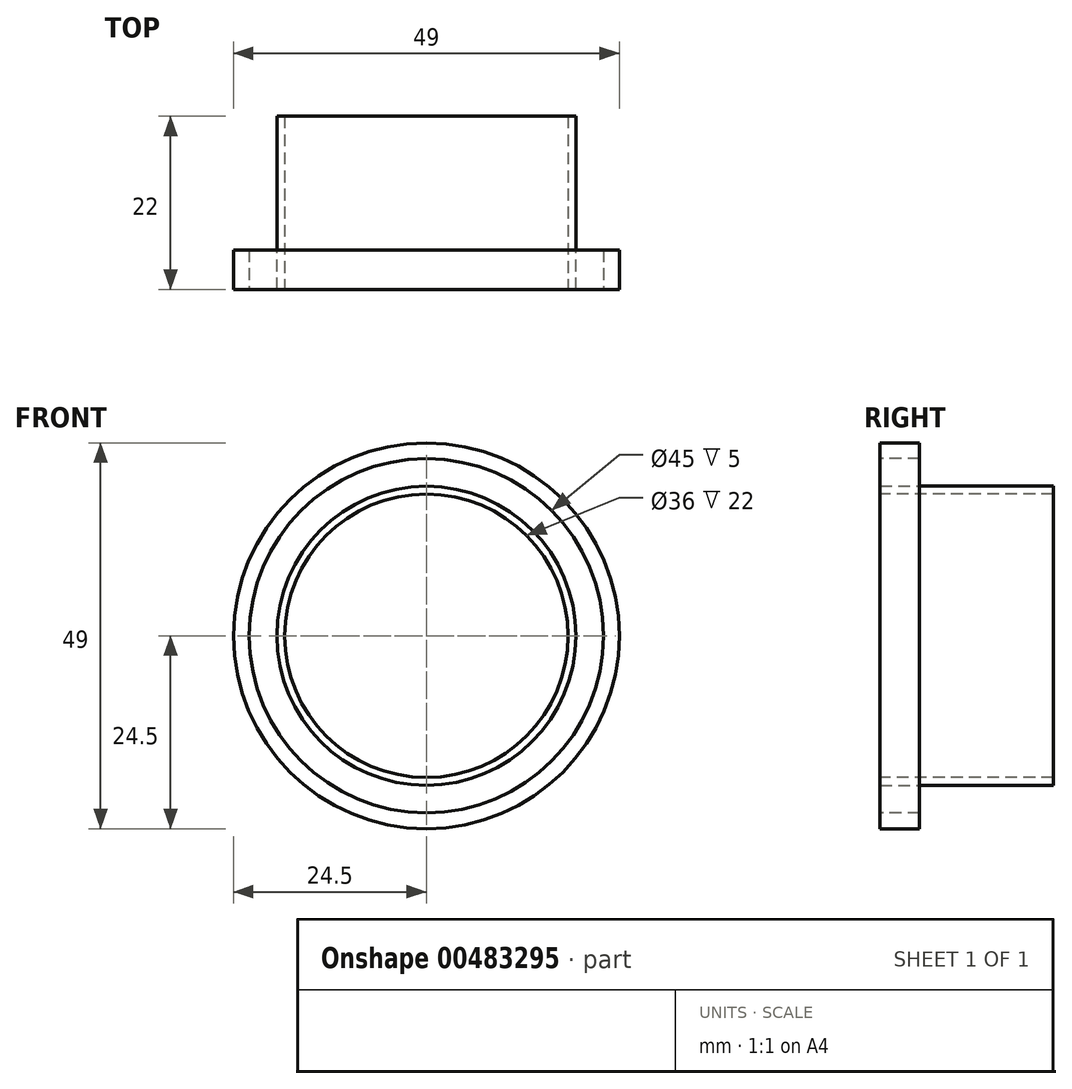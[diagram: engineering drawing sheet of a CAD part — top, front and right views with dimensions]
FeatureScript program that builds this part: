
annotation { "Feature Type Name" : "Feature", "Feature Type Description" : "" }
export const myFeature = defineFeature(function(context is Context, id is Id, definition is map)
    precondition{}
    {
        {
            var Q0;
            Q0=qCreatedBy(makeId("Front.planeOp"),FACE);
            var sketch = newSketch(context, id + "F0", { "sketchPlane" : qUnion([Q0])});
            skCircle(sketch, "E0", {"center": v(0, 0) * mm, "radius": 19 * mm});
            skSolve(sketch);
        }
        {
            var Q0;
            Q0 = qSketchRegion(id + "F0", true);
            extrude(context, id + "F1", {"entities" : qUnion([Q0]), "depth" : 22 * mm});
        }
        {
            var Q0;
            Q0=makeQuery(id+"F1.opExtrude","CAP_FACE",FACE,{"disambiguationData":[OSD([sQuery(id+"F0.wireOp",EDGE,"E0")])],"isStart":false});
            var sketch = newSketch(context, id + "F2", { "sketchPlane" : qUnion([Q0])});
            skCircle(sketch, "E1", {"center": v(0, 0) * mm, "radius": 18 * mm});
            skSolve(sketch);
        }
        {
            var Q0;
            Q0 = qSketchRegion(id + "F2", true);
            extrude(context, id + "F3", {"entities" : qUnion([Q0]), "operationType" : NewBodyOperationType.REMOVE, "endBound" : BoundingType.THROUGH_ALL, "oppositeDirection" : true, "depth" : 25.4 * mm});
        }
        {
            var Q0;
            Q0=makeQuery(id+"F1.opExtrude","CAP_FACE",FACE,{"disambiguationData":[OSD([sQuery(id+"F0.wireOp",EDGE,"E0")])],"isStart":false});
            var sketch = newSketch(context, id + "F4", { "sketchPlane" : qUnion([Q0])});
            skCircle(sketch, "E2", {"center": v(0, 0) * mm, "radius": 22.5 * mm});
            skCircle(sketch, "E3", {"center": v(0, 0) * mm, "radius": 24.5 * mm});
            skSolve(sketch);
        }
        {
            var Q0;
            Q0 = qSketchRegion(id + "F4", true);
            extrude(context, id + "F5", {"entities" : qUnion([Q0]), "oppositeDirection" : true, "depth" : 5 * mm});
        }
    });
